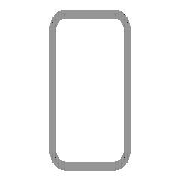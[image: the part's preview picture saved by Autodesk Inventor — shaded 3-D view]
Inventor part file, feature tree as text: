
AUTODESK INVENTOR PART (.ipt)
format: ipt  version: 2025 (Build 290162010, 162A)  size: 133,120 bytes
history: native  units: mm (DEFAULTED — no unit token found)
features: other x4, sketch x1, plane x1
ambient origin geometry x8: Origin, YZ Plane, XZ Plane, XY Plane, X Axis, Y Axis, Z Axis, Center Point
bodies: Solid1 (feature_tree), Body (feature_tree)
feature tree (6):
  parser-record x1  (decoder bookkeeping rows leaked as tree rows — omitted from the tree; the rows remain in map.json)
  other  "Driven Length"
  other  "Start Plane"
  other  "End Plane"
  sketch  "Sketch3"  dims[d3=2950.0mm d4=0.0mm d7=6.0mm d9=40.0mm d11=80.0mm d12=3.0mm d13=-0.0mm d14=2950.0mm d15=20.0mm d16=40.0mm d17=90.0deg d18=2950.0mm]
  plane  "Work Plane3"
